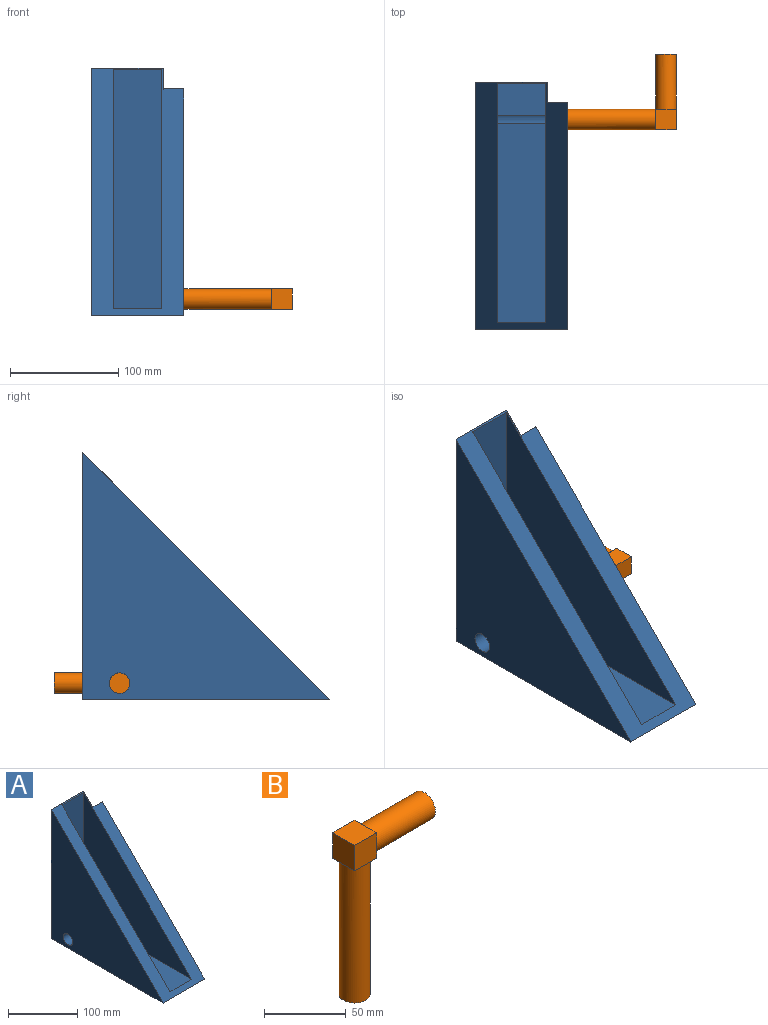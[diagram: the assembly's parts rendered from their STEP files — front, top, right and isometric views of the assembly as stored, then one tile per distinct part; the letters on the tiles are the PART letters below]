
ASSEMBLY  parts=2 mates=1
PART A: 13 faces, bbox 85.1x228.6x228.6 mm
  f0: plane 228.6x228.6mm, normal (-1,0,0), area 25844mm2, adj f6,f8,f9,f12
  f1: plane 184.54x44.45mm, normal (0,0,1), area 8202.8mm2, adj f3,f4,f6,f12
  f2: plane 44.45x29.6mm, normal (0,0,1), area 1315.7mm2, adj f3,f4,f5,f12
  f3: plane 220.98x220.98mm, normal (-1,0,0), area 24134mm2, adj f1,f2,f5,f6,f12
  f4: plane 220.98x220.98mm, normal (1,0,0), area 24134mm2, adj f1,f2,f5,f6,f12
  f5: plane 220.98x44.45mm, normal (0,-1,0), area 9822.6mm2, adj f2,f3,f4,f6
  f6: plane 228.6x228.6mm, normal (0,-0.71,0.71), area 13104.3mm2, adj f0,f1,f3,f4,f5,f7,f8,f9
  f7: plane 228.6x19.05mm, normal (1,0,0), area 4173.4mm2, adj f6,f8,f9,f10
  f8: plane 228.6x66.04mm, normal (0,1,0), area 15096.7mm2, adj f0,f6,f7,f9
  f9: plane 228.6x85.09mm, normal (0,0,-1), area 19088.7mm2, adj f0,f6,f7,f8,f10,f11
  f10: plane 209.55x19.05mm, normal (0,1,0), area 3991.9mm2, adj f6,f7,f9,f11
  f11: plane 209.55x209.55mm, normal (1,0,0), area 21670.6mm2, adj f6,f9,f10,f12
  f12: cylinder r=9.53mm len=85.09mm, axis (1,0,0), area 2743.1mm2, adj f0,f1,f2,f3,f4,f11
PART B: 16 faces, bbox 69.9x19.1x120.7 mm
  f0: plane 9.53x9.53mm, normal (1,0,0), area 19.5mm2, adj f5,f12,f14
  f1: plane 9.53x9.53mm, normal (1,0,0), area 19.5mm2, adj f12,f13,f14
  f2: plane 9.53x9.53mm, normal (1,0,0), area 19.5mm2, adj f10,f13,f14
  f3: cylinder r=9.53mm len=101.6mm, axis (0,0,-1), area 6080.5mm2, adj f4,f5,f6,f7,f8
  f4: plane 19.05x19.05mm, normal (0,0,-1), area 285mm2, adj f3
  f5: plane 9.53x9.53mm, normal (0,0,-1), area 19.5mm2, adj f0,f3,f12
  f6: plane 9.53x9.53mm, normal (0,0,-1), area 19.5mm2, adj f3,f9,f12
  f7: plane 9.53x9.53mm, normal (0,0,-1), area 19.5mm2, adj f3,f9,f10
  f8: plane 9.53x9.53mm, normal (0,0,-1), area 19.5mm2, adj f3,f10,f11
  f9: plane 19.05x19.05mm, normal (-1,0,0), area 362.9mm2, adj f6,f7,f10,f12,f13
  f10: plane 19.05x19.05mm, normal (0,-1,0), area 362.9mm2, adj f2,f7,f8,f9,f11,f13
  f11: plane 9.53x9.53mm, normal (1,0,0), area 19.5mm2, adj f8,f10,f14
  f12: plane 19.05x19.05mm, normal (0,1,0), area 362.9mm2, adj f0,f1,f5,f6,f9,f13
  f13: plane 19.05x19.05mm, normal (0,0,1), area 362.9mm2, adj f1,f2,f9,f10,f12
  f14: cylinder r=9.53mm len=50.8mm, axis (-1,0,0), area 3040.2mm2, adj f0,f1,f2,f11,f15
  f15: plane 19.05x19.05mm, normal (1,0,0), area 285mm2, adj f14
PLACE A t=(112.98,53.75,-169.85)mm
PLACE B rot(axis=(0.58,0.58,0.58),120deg) t=(111.71,19.46,-154.61)mm
MATE fastened A.f12 <-> B.f3  axis (-1,0,0) through (111.71,19.46,-154.61)mm
